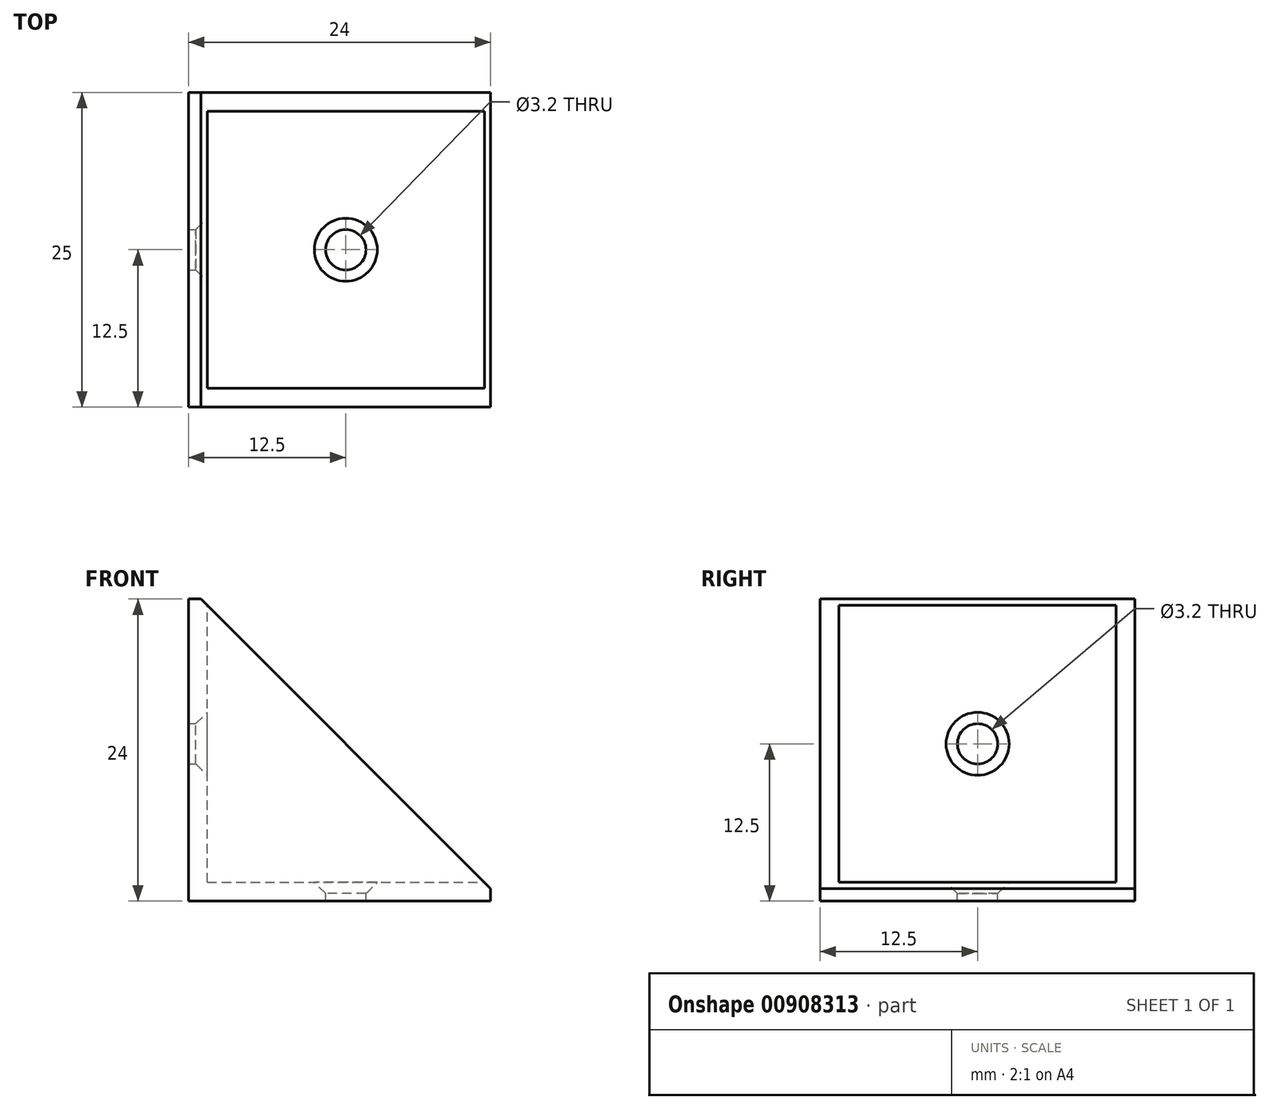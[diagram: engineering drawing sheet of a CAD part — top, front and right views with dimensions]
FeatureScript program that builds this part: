
annotation { "Feature Type Name" : "Feature", "Feature Type Description" : "" }
export const myFeature = defineFeature(function(context is Context, id is Id, definition is map)
    precondition{}
    {
        {
            var Q0;
            Q0=qCreatedBy(makeId("Front.planeOp"),FACE);
            var sketch = newSketch(context, id + "F0", { "sketchPlane" : qUnion([Q0])});
            skLineSegment(sketch, "E0", {"start": v(0, 0) * mm, "end": v(0, 25) * mm});
            skLineSegment(sketch, "E1", {"start": v(0, 0) * mm, "end": v(25, 0) * mm});
            skLineSegment(sketch, "E2", {"start": v(25, 0) * mm, "end": v(0, 25) * mm});
            skSolve(sketch);
        }
        {
            var Q0;
            Q0=makeQuery(id+"F0.imprint","IMPRINT",FACE,{"disambiguationData":[TD([[makeQuery(id+"F0.imprint","IMPRINT",EDGE,{"derivedFrom":sQuery(id+"F0.wireOp",EDGE,"E0")}),-1.0]])]});
            extrude(context, id + "F1", {"entities" : qUnion([Q0]), "depth" : 25 * mm, "offsetDistance" : 25 * mm});
        }
        {
            var Q0;
            Q0=makeQuery(id+"F1.opExtrude","SWEPT_FACE",FACE,{"disambiguationData":[OSD([sQuery(id+"F0.wireOp",EDGE,"E2")])]});
            shell(context, id + "F2", {"entities" : qUnion([Q0]), "thickness" : 1.5 * mm});
        }
        {
            var Q0;
            Q0=makeQuery(id+"F1.opExtrude","SWEPT_EDGE",EDGE,{"disambiguationData":[OSD([sQuery(id+"F0.wireOp",EDGE,"E0"),sQuery(id+"F0.wireOp",EDGE,"E2")])]});
            chamfer(context, id + "F3", {"entities" : qUnion([Q0]), "chamferType" : ChamferType.OFFSET_ANGLE, "width" : 1 * mm, "oppositeDirection" : false, "angle" : 90 * degree, "tangentPropagation" : true});
        }
        {
            var Q0;
            Q0=makeQuery(id+"F1.opExtrude","SWEPT_EDGE",EDGE,{"disambiguationData":[OSD([sQuery(id+"F0.wireOp",EDGE,"E1"),sQuery(id+"F0.wireOp",EDGE,"E2")])]});
            chamfer(context, id + "F4", {"entities" : qUnion([Q0]), "chamferType" : ChamferType.OFFSET_ANGLE, "width" : 1.41 * mm, "oppositeDirection" : false, "angle" : 45 * degree});
        }
        {
            var Q0;
            Q0=makeQuery(id+"F2.opShell","OFFSET_FACE",FACE,{"disambiguationData":[OSD([sQuery(id+"F0.wireOp",EDGE,"E1")])]});
            var sketch = newSketch(context, id + "F5", { "sketchPlane" : qUnion([Q0])});
            skPoint(sketch, "E3", {"position": v(12.5, -12.5) * mm});
            skSolve(sketch);
        }
        {
            var Q0;
            Q0=sQuery(id+"F5.wireOp",VERTEX,"E3");
            var Q1;
            Q1=makeQuery(id+"F1.opExtrude","SWEPT_BODY",BODY,{"disambiguationData":[OSD([sQuery(id+"F0.wireOp",EDGE,"E0"),sQuery(id+"F0.wireOp",EDGE,"E1"),sQuery(id+"F0.wireOp",EDGE,"E2")])]});
            hole(context, id + "F6", {"style" : HoleStyle.C_SINK, "endStyle" : HoleEndStyle.THROUGH, "holeDiameter" : 3.2 * mm, "cSinkDiameter" : 5 * mm, "cSinkAngle" : 90 * degree, "majorDiameter" : 5 * mm, "isTappedThrough" : true, "tappedDepth" : 12 * mm, "tapClearance" : 3, "locations" : qUnion([Q0]), "scope" : qUnion([Q1])});
        }
        {
            var Q0;
            Q0=makeQuery(id+"F2.opShell","OFFSET_FACE",FACE,{"disambiguationData":[OSD([sQuery(id+"F0.wireOp",EDGE,"E0")])]});
            var sketch = newSketch(context, id + "F7", { "sketchPlane" : qUnion([Q0])});
            skPoint(sketch, "E4", {"position": v(-12.5, 12.5) * mm});
            skSolve(sketch);
        }
        {
            var Q0;
            Q0=sQuery(id+"F7.wireOp",VERTEX,"E4");
            var Q1;
            Q1=makeQuery(id+"F1.opExtrude","SWEPT_BODY",BODY,{"disambiguationData":[OSD([sQuery(id+"F0.wireOp",EDGE,"E0"),sQuery(id+"F0.wireOp",EDGE,"E1"),sQuery(id+"F0.wireOp",EDGE,"E2")])]});
            hole(context, id + "F8", {"style" : HoleStyle.C_SINK, "endStyle" : HoleEndStyle.THROUGH, "holeDiameter" : 3.2 * mm, "cSinkDiameter" : 5 * mm, "cSinkAngle" : 90 * degree, "majorDiameter" : 5 * mm, "isTappedThrough" : true, "tappedDepth" : 12 * mm, "tapClearance" : 3, "locations" : qUnion([Q0]), "scope" : qUnion([Q1])});
        }
    });
